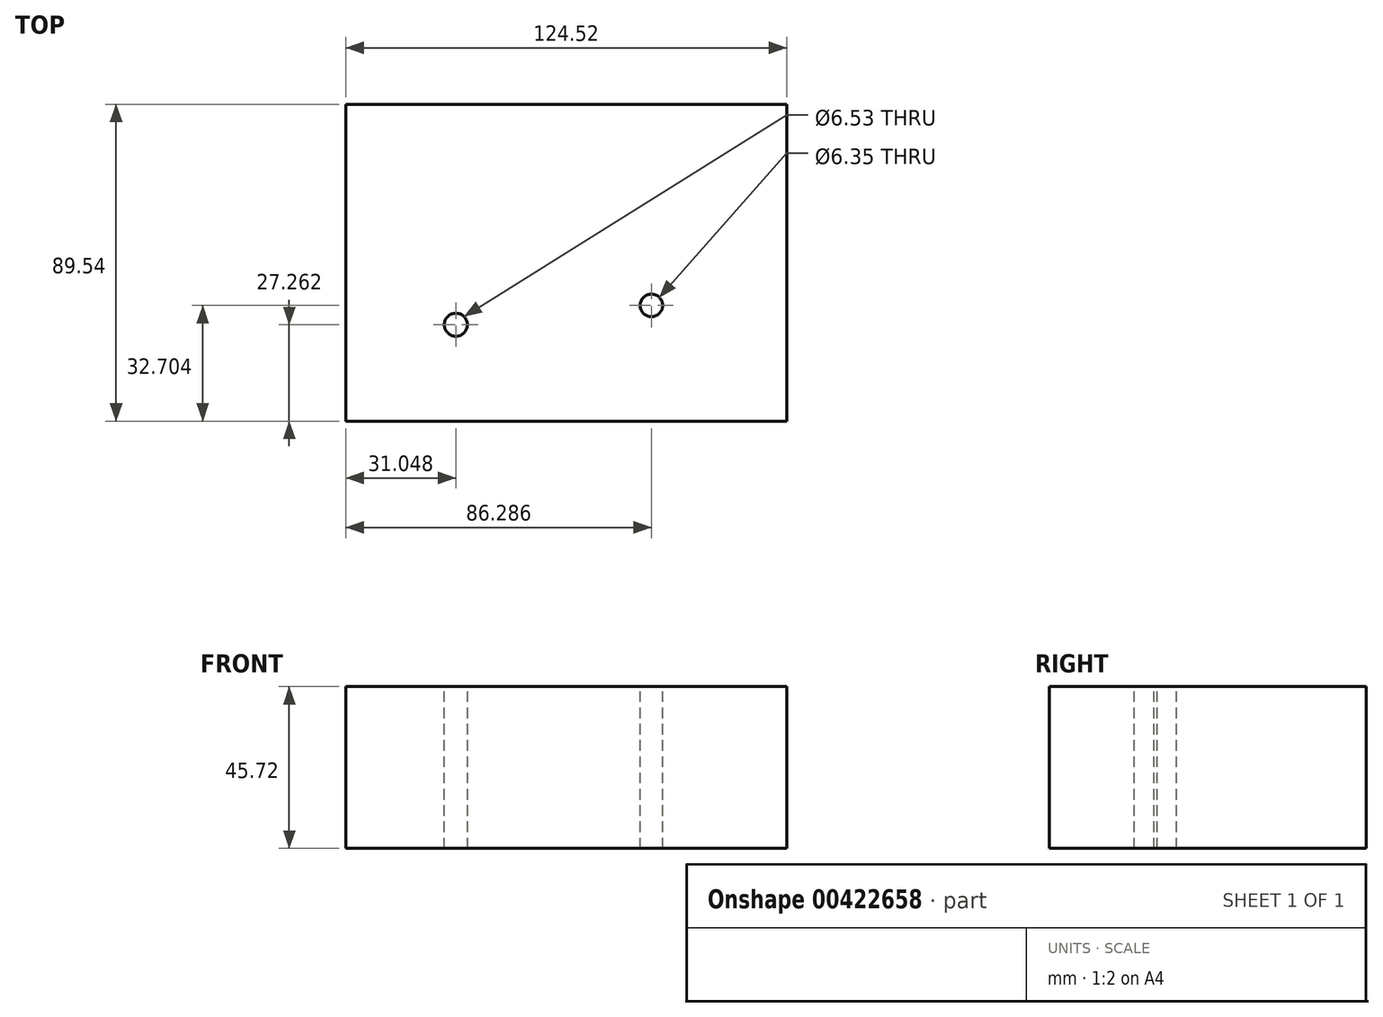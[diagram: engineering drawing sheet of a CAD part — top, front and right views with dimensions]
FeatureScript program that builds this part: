
annotation { "Feature Type Name" : "Feature", "Feature Type Description" : "" }
export const myFeature = defineFeature(function(context is Context, id is Id, definition is map)
    precondition{}
    {
        {
            var Q0;
            Q0=qCreatedBy(makeId("Top.planeOp"),FACE);
            var sketch = newSketch(context, id + "F0", { "sketchPlane" : qUnion([Q0])});
            skLineSegment(sketch, "E0.bottom", {"start": v(-53.69, 45.03) * mm, "end": v(70.83, 45.03) * mm});
            skLineSegment(sketch, "E0.top", {"start": v(-53.69, -44.5) * mm, "end": v(70.83, -44.5) * mm});
            skLineSegment(sketch, "E0.left", {"start": v(-53.69, 45.03) * mm, "end": v(-53.69, -44.5) * mm});
            skLineSegment(sketch, "E0.right", {"start": v(70.83, 45.03) * mm, "end": v(70.83, -44.5) * mm});
            skSolve(sketch);
        }
        {
            var Q0;
            Q0=makeQuery(id+"F0.imprint","IMPRINT",FACE,{"disambiguationData":[TD([[makeQuery(id+"F0.imprint","IMPRINT",EDGE,{"derivedFrom":sQuery(id+"F0.wireOp",EDGE,"E0.bottom")}),-1.0]])]});
            extrude(context, id + "F1", {"entities" : qUnion([Q0]), "depth" : 45.72 * mm});
        }
        {
            var Q0;
            Q0=makeQuery(id+"F1.opExtrude","CAP_FACE",FACE,{"disambiguationData":[OSD([sQuery(id+"F0.wireOp",EDGE,"E0.bottom"),sQuery(id+"F0.wireOp",EDGE,"E0.top"),sQuery(id+"F0.wireOp",EDGE,"E0.left"),sQuery(id+"F0.wireOp",EDGE,"E0.right")])],"isStart":false});
            var sketch = newSketch(context, id + "F2", { "sketchPlane" : qUnion([Q0])});
            skPoint(sketch, "E1", {"position": v(52.4, -17.25) * mm});
            skPoint(sketch, "E2", {"position": v(48.85, 22.84) * mm});
            skPoint(sketch, "E3", {"position": v(-21.36, 17.04) * mm});
            skPoint(sketch, "E4", {"position": v(-22.64, -17.25) * mm});
            skSolve(sketch);
        }
        {
            var Q0;
            Q0=sQuery(id+"F2.wireOp",VERTEX,"E4");
            var Q1;
            Q1=makeQuery(id+"F1.opExtrude","SWEPT_BODY",BODY,{"disambiguationData":[OSD([sQuery(id+"F0.wireOp",EDGE,"E0.bottom"),sQuery(id+"F0.wireOp",EDGE,"E0.top"),sQuery(id+"F0.wireOp",EDGE,"E0.left"),sQuery(id+"F0.wireOp",EDGE,"E0.right")])]});
            hole(context, id + "F3", {"style" : HoleStyle.SIMPLE, "endStyle" : HoleEndStyle.THROUGH, "standardTappedOrClearance" : lookupTablePath({ "standard" : "ANSI", "fit" : "Close", "size" : "1/4", "type" : "Clearance" }), "standardBlindInLast" : lookupTablePath({ "fit" : "Close", "standard" : "ANSI", "size" : "1/4", "type" : "Clearance" }), "holeDiameter" : 6.53 * mm, "isTappedThrough" : true, "tappedDepth" : 12.7 * mm, "tapClearance" : 3, "locations" : qUnion([Q0]), "scope" : qUnion([Q1])});
        }
        {
            var Q0;
            Q0=makeQuery(id+"F1.opExtrude","CAP_FACE",FACE,{"disambiguationData":[OSD([sQuery(id+"F0.wireOp",EDGE,"E0.bottom"),sQuery(id+"F0.wireOp",EDGE,"E0.top"),sQuery(id+"F0.wireOp",EDGE,"E0.left"),sQuery(id+"F0.wireOp",EDGE,"E0.right")])],"isStart":false});
            var sketch = newSketch(context, id + "F4", { "sketchPlane" : qUnion([Q0])});
            skPoint(sketch, "E5", {"position": v(32.6, -11.8) * mm});
            skPoint(sketch, "E6", {"position": v(32.64, 25.9) * mm});
            skPoint(sketch, "E7", {"position": v(-25.37, 18.18) * mm});
            skSolve(sketch);
        }
        {
            var Q0;
            Q0=sQuery(id+"F4.wireOp",VERTEX,"E5");
            var Q1;
            Q1=makeQuery(id+"F1.opExtrude","SWEPT_BODY",BODY,{"disambiguationData":[OSD([sQuery(id+"F0.wireOp",EDGE,"E0.bottom"),sQuery(id+"F0.wireOp",EDGE,"E0.top"),sQuery(id+"F0.wireOp",EDGE,"E0.left"),sQuery(id+"F0.wireOp",EDGE,"E0.right")])]});
            hole(context, id + "F5", {"style" : HoleStyle.SIMPLE, "endStyle" : HoleEndStyle.THROUGH, "holeDiameter" : 6.35 * mm, "isTappedThrough" : true, "tappedDepth" : 12.7 * mm, "tapClearance" : 3, "locations" : qUnion([Q0]), "scope" : qUnion([Q1])});
        }
    });
